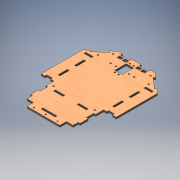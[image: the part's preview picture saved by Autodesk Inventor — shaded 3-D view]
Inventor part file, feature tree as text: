
AUTODESK INVENTOR PART (.ipt)
format: ipt  version: 2019 (Build 230136000, 136)  size: 332,288 bytes
history: native  units: mm
features: sketch x5, extrude x3, hole x2, other x1
ambient origin geometry x8: Origin, YZ Plane, XZ Plane, XY Plane, X Axis, Y Axis, Z Axis, Center Point
bodies: Body1 (feature_tree)
feature tree (11):
  other  "Твердое тело1"
  extrude  "Выдавливание1"  Depth=160.0mm
  hole  "Отверстие1"  [1 undecoded]
  extrude  "Выдавливание2"  Depth=65.2mm
  extrude  "Выдавливание3"  Depth=80.0mm
  hole  "Отверстие2"  [1 undecoded]
  sketch  "Эскиз1"
  sketch  "Эскиз3"
  sketch  "Эскиз4"
  sketch  "Эскиз5"
  sketch  "Эскиз6"
note: 2 required parameter values undecoded (feature->parameter linkage not recoverable at this tier; creation-order binding heuristic only, values carry confidence <= 0.55)
